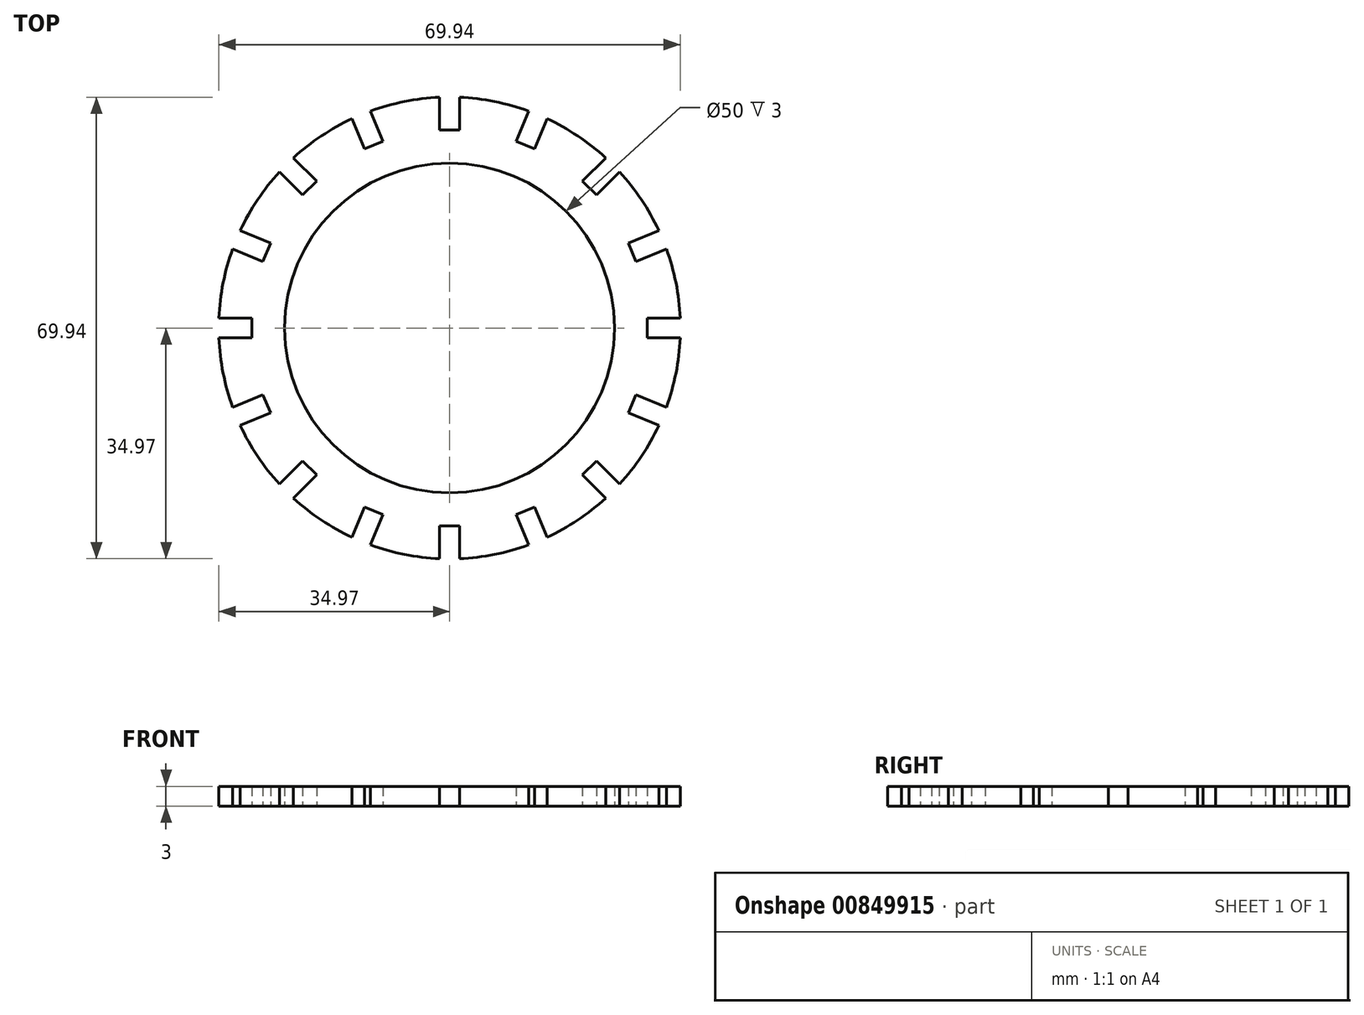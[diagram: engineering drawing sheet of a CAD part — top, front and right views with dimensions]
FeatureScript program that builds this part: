
annotation { "Feature Type Name" : "Feature", "Feature Type Description" : "" }
export const myFeature = defineFeature(function(context is Context, id is Id, definition is map)
    precondition{}
    {
        {
            var Q0;
            Q0=qCreatedBy(makeId("Top.planeOp"),FACE);
            var sketch = newSketch(context, id + "F0", { "sketchPlane" : qUnion([Q0])});
            skCircle(sketch, "E0", {"center": v(0, 0) * mm, "radius": 25 * mm});
            skCircle(sketch, "E1", {"center": v(0, 0) * mm, "radius": 35 * mm});
            skLineSegment(sketch, "E2", {"start": v(0, -30) * mm, "end": v(-1.5, -30) * mm});
            skLineSegment(sketch, "E3", {"start": v(-1.5, -30) * mm, "end": v(1.5, -30) * mm});
            skLineSegment(sketch, "E4", {"start": v(1.5, -30) * mm, "end": v(1.5, -34.97) * mm});
            skLineSegment(sketch, "E5", {"start": v(-1.5, -30) * mm, "end": v(-1.5, -34.97) * mm});
            skLineSegment(sketch, "E6.1.0", {"start": v(10.1, -28.3) * mm, "end": v(12.87, -27.14) * mm});
            skLineSegment(sketch, "E6.1.1", {"start": v(10.1, -28.3) * mm, "end": v(12, -32.88) * mm});
            skLineSegment(sketch, "E6.1.2", {"start": v(12.87, -27.14) * mm, "end": v(14.77, -31.73) * mm});
            skLineSegment(sketch, "E6.2.0", {"start": v(20.15, -22.27) * mm, "end": v(22.27, -20.15) * mm});
            skLineSegment(sketch, "E6.2.1", {"start": v(20.15, -22.27) * mm, "end": v(23.67, -25.79) * mm});
            skLineSegment(sketch, "E6.2.2", {"start": v(22.27, -20.15) * mm, "end": v(25.79, -23.67) * mm});
            skLineSegment(sketch, "E6.3.0", {"start": v(27.14, -12.87) * mm, "end": v(28.3, -10.1) * mm});
            skLineSegment(sketch, "E6.3.1", {"start": v(27.14, -12.87) * mm, "end": v(31.73, -14.77) * mm});
            skLineSegment(sketch, "E6.3.2", {"start": v(28.3, -10.1) * mm, "end": v(32.88, -12) * mm});
            skLineSegment(sketch, "E6.4.0", {"start": v(30, -1.5) * mm, "end": v(30, 1.5) * mm});
            skLineSegment(sketch, "E6.4.1", {"start": v(30, -1.5) * mm, "end": v(34.97, -1.5) * mm});
            skLineSegment(sketch, "E6.4.2", {"start": v(30, 1.5) * mm, "end": v(34.97, 1.5) * mm});
            skLineSegment(sketch, "E6.5.0", {"start": v(28.3, 10.1) * mm, "end": v(27.14, 12.87) * mm});
            skLineSegment(sketch, "E6.5.1", {"start": v(28.3, 10.1) * mm, "end": v(32.88, 12) * mm});
            skLineSegment(sketch, "E6.5.2", {"start": v(27.14, 12.87) * mm, "end": v(31.73, 14.77) * mm});
            skLineSegment(sketch, "E6.6.0", {"start": v(22.27, 20.15) * mm, "end": v(20.15, 22.27) * mm});
            skLineSegment(sketch, "E6.6.1", {"start": v(22.27, 20.15) * mm, "end": v(25.79, 23.67) * mm});
            skLineSegment(sketch, "E6.6.2", {"start": v(20.15, 22.27) * mm, "end": v(23.67, 25.79) * mm});
            skLineSegment(sketch, "E6.7.0", {"start": v(12.87, 27.14) * mm, "end": v(10.1, 28.3) * mm});
            skLineSegment(sketch, "E6.7.1", {"start": v(12.87, 27.14) * mm, "end": v(14.77, 31.73) * mm});
            skLineSegment(sketch, "E6.7.2", {"start": v(10.1, 28.3) * mm, "end": v(12, 32.88) * mm});
            skLineSegment(sketch, "E6.8.0", {"start": v(1.5, 30) * mm, "end": v(-1.5, 30) * mm});
            skLineSegment(sketch, "E6.8.1", {"start": v(1.5, 30) * mm, "end": v(1.5, 34.97) * mm});
            skLineSegment(sketch, "E6.8.2", {"start": v(-1.5, 30) * mm, "end": v(-1.5, 34.97) * mm});
            skLineSegment(sketch, "E6.9.0", {"start": v(-10.1, 28.3) * mm, "end": v(-12.87, 27.14) * mm});
            skLineSegment(sketch, "E6.9.1", {"start": v(-10.1, 28.3) * mm, "end": v(-12, 32.88) * mm});
            skLineSegment(sketch, "E6.9.2", {"start": v(-12.87, 27.14) * mm, "end": v(-14.77, 31.73) * mm});
            skLineSegment(sketch, "E6.10.0", {"start": v(-20.15, 22.27) * mm, "end": v(-22.27, 20.15) * mm});
            skLineSegment(sketch, "E6.10.1", {"start": v(-20.15, 22.27) * mm, "end": v(-23.67, 25.79) * mm});
            skLineSegment(sketch, "E6.10.2", {"start": v(-22.27, 20.15) * mm, "end": v(-25.79, 23.67) * mm});
            skLineSegment(sketch, "E6.11.0", {"start": v(-27.14, 12.87) * mm, "end": v(-28.3, 10.1) * mm});
            skLineSegment(sketch, "E6.11.1", {"start": v(-27.14, 12.87) * mm, "end": v(-31.73, 14.77) * mm});
            skLineSegment(sketch, "E6.11.2", {"start": v(-28.3, 10.1) * mm, "end": v(-32.88, 12) * mm});
            skLineSegment(sketch, "E6.12.0", {"start": v(-30, 1.5) * mm, "end": v(-30, -1.5) * mm});
            skLineSegment(sketch, "E6.12.1", {"start": v(-30, 1.5) * mm, "end": v(-34.97, 1.5) * mm});
            skLineSegment(sketch, "E6.12.2", {"start": v(-30, -1.5) * mm, "end": v(-34.97, -1.5) * mm});
            skLineSegment(sketch, "E6.13.0", {"start": v(-28.3, -10.1) * mm, "end": v(-27.14, -12.87) * mm});
            skLineSegment(sketch, "E6.13.1", {"start": v(-28.3, -10.1) * mm, "end": v(-32.88, -12) * mm});
            skLineSegment(sketch, "E6.13.2", {"start": v(-27.14, -12.87) * mm, "end": v(-31.73, -14.77) * mm});
            skLineSegment(sketch, "E6.14.0", {"start": v(-22.27, -20.15) * mm, "end": v(-20.15, -22.27) * mm});
            skLineSegment(sketch, "E6.14.1", {"start": v(-22.27, -20.15) * mm, "end": v(-25.79, -23.67) * mm});
            skLineSegment(sketch, "E6.14.2", {"start": v(-20.15, -22.27) * mm, "end": v(-23.67, -25.79) * mm});
            skLineSegment(sketch, "E6.15.0", {"start": v(-12.87, -27.14) * mm, "end": v(-10.1, -28.3) * mm});
            skLineSegment(sketch, "E6.15.1", {"start": v(-12.87, -27.14) * mm, "end": v(-14.77, -31.73) * mm});
            skLineSegment(sketch, "E6.15.2", {"start": v(-10.1, -28.3) * mm, "end": v(-12, -32.88) * mm});
            skSolve(sketch);
        }
        {
            var Q0;
            Q0=makeQuery(id+"F0.imprint","IMPRINT",FACE,{"disambiguationData":[TD([[makeQuery(id+"F0.imprint","IMPRINT",EDGE,{"derivedFrom":sQuery(id+"F0.wireOp",EDGE,"E0")}),-1.0]])]});
            extrude(context, id + "F1", {"entities" : qUnion([Q0]), "depth" : 3 * mm, "offsetDistance" : 25 * mm});
        }
    });
